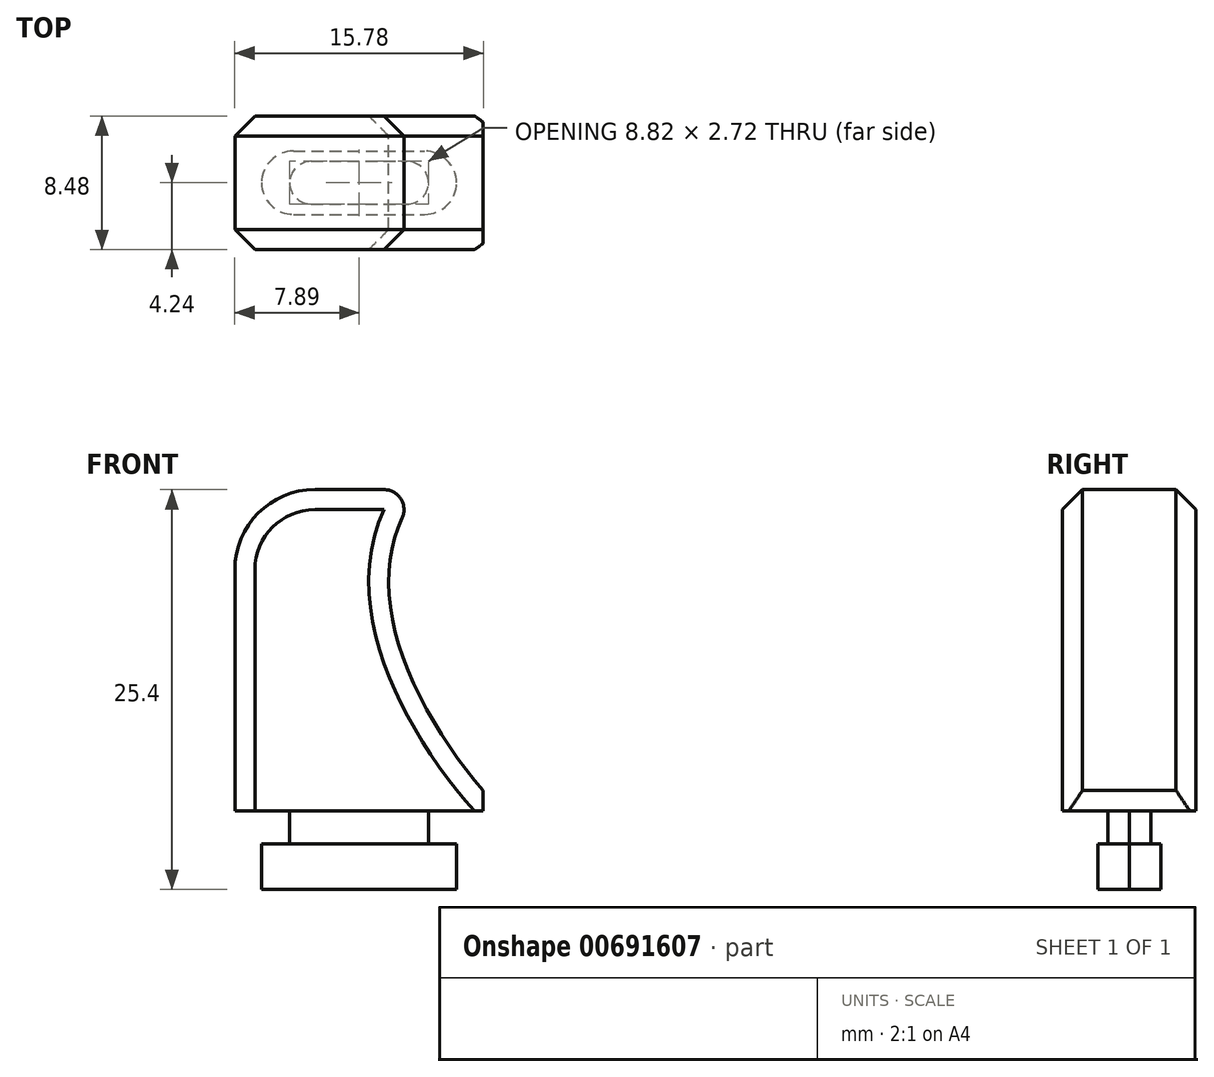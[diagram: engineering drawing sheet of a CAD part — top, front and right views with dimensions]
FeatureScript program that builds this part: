
annotation { "Feature Type Name" : "Feature", "Feature Type Description" : "" }
export const myFeature = defineFeature(function(context is Context, id is Id, definition is map)
    precondition{}
    {
        {
            var Q0;
            Q0=qCreatedBy(makeId("Top.planeOp"),FACE);
            var sketch = newSketch(context, id + "F0", { "sketchPlane" : qUnion([Q0])});
            skLineSegment(sketch, "E0.bottom", {"start": v(-6.2, -2) * mm, "end": v(6.2, -2) * mm});
            skLineSegment(sketch, "E0.top", {"start": v(-6.2, 2) * mm, "end": v(6.2, 2) * mm});
            skLineSegment(sketch, "E0.left", {"start": v(-6.2, -2) * mm, "end": v(-6.2, 2) * mm});
            skLineSegment(sketch, "E0.right", {"start": v(6.2, -2) * mm, "end": v(6.2, 2) * mm});
            skPoint(sketch, "E0.middle", {"position": v(0, 0) * mm});
            skSolve(sketch);
        }
        {
            var Q0;
            Q0=makeQuery(id+"F0.imprint","IMPRINT",FACE,{"disambiguationData":[TD([[makeQuery(id+"F0.imprint","IMPRINT",EDGE,{"derivedFrom":sQuery(id+"F0.wireOp",EDGE,"E0.bottom")}),1.0]])]});
            extrude(context, id + "F1", {"entities" : qUnion([Q0]), "depth" : 2.9 * mm, "offsetDistance" : 25.4 * mm});
        }
        {
            var Q0;
            Q0=makeQuery(id+"F1.opExtrude","SWEPT_EDGE",EDGE,{"disambiguationData":[OSD([sQuery(id+"F0.wireOp",EDGE,"E0.top"),sQuery(id+"F0.wireOp",EDGE,"E0.left")])]});
            var Q1;
            Q1=makeQuery(id+"F1.opExtrude","SWEPT_EDGE",EDGE,{"disambiguationData":[OSD([sQuery(id+"F0.wireOp",EDGE,"E0.bottom"),sQuery(id+"F0.wireOp",EDGE,"E0.left")])]});
            fillet(context, id + "F2", {"entities" : qUnion([Q0, Q1]), "radius" : 2.03 * mm, "tangentPropagation" : true, "allowEdgeOverflow" : false});
        }
        {
            var Q0;
            Q0=makeQuery(id+"F1.opExtrude","SWEPT_EDGE",EDGE,{"disambiguationData":[OSD([sQuery(id+"F0.wireOp",EDGE,"E0.top"),sQuery(id+"F0.wireOp",EDGE,"E0.right")])]});
            var Q1;
            Q1=makeQuery(id+"F1.opExtrude","SWEPT_EDGE",EDGE,{"disambiguationData":[OSD([sQuery(id+"F0.wireOp",EDGE,"E0.bottom"),sQuery(id+"F0.wireOp",EDGE,"E0.right")])]});
            fillet(context, id + "F3", {"entities" : qUnion([Q0, Q1]), "radius" : 2.03 * mm, "tangentPropagation" : true, "allowEdgeOverflow" : false});
        }
        {
            var Q0;
            Q0=makeQuery(id+"F1.opExtrude","CAP_FACE",FACE,{"disambiguationData":[OSD([sQuery(id+"F0.wireOp",EDGE,"E0.bottom"),sQuery(id+"F0.wireOp",EDGE,"E0.top"),sQuery(id+"F0.wireOp",EDGE,"E0.left"),sQuery(id+"F0.wireOp",EDGE,"E0.right")])],"isStart":false});
            var sketch = newSketch(context, id + "F4", { "sketchPlane" : qUnion([Q0])});
            skLineSegment(sketch, "E1.bottom", {"start": v(-4.4, -1.36) * mm, "end": v(4.4, -1.36) * mm});
            skLineSegment(sketch, "E1.top", {"start": v(-4.4, 1.36) * mm, "end": v(4.4, 1.36) * mm});
            skLineSegment(sketch, "E1.left", {"start": v(-4.4, -1.36) * mm, "end": v(-4.4, 1.36) * mm});
            skLineSegment(sketch, "E1.right", {"start": v(4.4, -1.36) * mm, "end": v(4.4, 1.36) * mm});
            skPoint(sketch, "E1.middle", {"position": v(0, 0) * mm});
            skSolve(sketch);
        }
        {
            var Q0;
            Q0=makeQuery(id+"F4.imprint","IMPRINT",FACE,{"disambiguationData":[TD([[makeQuery(id+"F4.imprint","IMPRINT",EDGE,{"derivedFrom":sQuery(id+"F4.wireOp",EDGE,"E1.bottom")}),1.0]])]});
            extrude(context, id + "F5", {"entities" : qUnion([Q0]), "operationType" : NewBodyOperationType.ADD, "depth" : 2.1 * mm, "offsetDistance" : 25.4 * mm});
        }
        {
            var Q0;
            Q0=makeQuery(id+"F5.opExtrude","SWEPT_EDGE",EDGE,{"disambiguationData":[OSD([sQuery(id+"F4.wireOp",EDGE,"E1.bottom"),sQuery(id+"F4.wireOp",EDGE,"E1.left")])]});
            var Q1;
            Q1=makeQuery(id+"F5.opExtrude","SWEPT_EDGE",EDGE,{"disambiguationData":[OSD([sQuery(id+"F4.wireOp",EDGE,"E1.top"),sQuery(id+"F4.wireOp",EDGE,"E1.left")])]});
            fillet(context, id + "F6", {"entities" : qUnion([Q0, Q1]), "radius" : 1.37 * mm, "tangentPropagation" : true, "allowEdgeOverflow" : false});
        }
        {
            var Q0;
            Q0=makeQuery(id+"F5.opExtrude","SWEPT_EDGE",EDGE,{"disambiguationData":[OSD([sQuery(id+"F4.wireOp",EDGE,"E1.top"),sQuery(id+"F4.wireOp",EDGE,"E1.right")])]});
            var Q1;
            Q1=makeQuery(id+"F5.opExtrude","SWEPT_EDGE",EDGE,{"disambiguationData":[OSD([sQuery(id+"F4.wireOp",EDGE,"E1.bottom"),sQuery(id+"F4.wireOp",EDGE,"E1.right")])]});
            fillet(context, id + "F7", {"entities" : qUnion([Q0, Q1]), "radius" : 1.37 * mm, "tangentPropagation" : true, "allowEdgeOverflow" : false});
        }
        {
            var Q0;
            Q0=qCreatedBy(makeId("Top.planeOp"),FACE);
            var sketch = newSketch(context, id + "F8", { "sketchPlane" : qUnion([Q0])});
            skLineSegment(sketch, "E2.bottom", {"start": v(-7.89, -4.24) * mm, "end": v(7.89, -4.24) * mm});
            skLineSegment(sketch, "E2.top", {"start": v(-7.89, 4.24) * mm, "end": v(7.89, 4.24) * mm});
            skLineSegment(sketch, "E2.left", {"start": v(-7.89, -4.24) * mm, "end": v(-7.89, 4.24) * mm});
            skLineSegment(sketch, "E2.right", {"start": v(7.89, -4.24) * mm, "end": v(7.89, 4.24) * mm});
            skPoint(sketch, "E2.middle", {"position": v(0, 0) * mm});
            skSolve(sketch);
        }
        {
            var Q0;
            Q0=makeQuery(id+"F8.imprint","IMPRINT",FACE,{"disambiguationData":[TD([[makeQuery(id+"F8.imprint","IMPRINT",EDGE,{"derivedFrom":sQuery(id+"F8.wireOp",EDGE,"E2.bottom")}),1.0]])]});
            extrude(context, id + "F9", {"entities" : qUnion([Q0]), "operationType" : NewBodyOperationType.ADD, "depth" : 25.4 * mm, "offsetDistance" : 25.4 * mm, "hasSecondDirection" : true, "secondDirectionOppositeDirection" : false, "secondDirectionDepth" : 5 * mm});
        }
        {
            var Q0;
            Q0=qCreatedBy(makeId("Front.planeOp"),FACE);
            var sketch = newSketch(context, id + "F10", { "sketchPlane" : qUnion([Q0])});
            skFitSpline(sketch, "E3", {"points": [v(4.8, 26.41) * mm, v(2.47, 15.73) * mm, v(11.26, 3.33) * mm, v(13.6, 3.08) * mm, v(13.85, 5.6) * mm, v(12.97, 27.36) * mm, v(4.8, 26.41) * mm]});
            skSolve(sketch);
        }
        {
            var Q0;
            Q0=makeQuery(id+"F10.imprint","IMPRINT",FACE,{"disambiguationData":[TD([[makeQuery(id+"F10.imprint","IMPRINT",EDGE,{"derivedFrom":sQuery(id+"F10.wireOp",EDGE,"E3")}),1.0]])]});
            extrude(context, id + "F11", {"entities" : qUnion([Q0]), "operationType" : NewBodyOperationType.REMOVE, "oppositeDirection" : true, "depth" : 25.4 * mm, "offsetDistance" : 25.4 * mm, "hasSecondDirection" : true, "secondDirectionOppositeDirection" : false, "secondDirectionDepth" : 25.4 * mm});
        }
        {
            var Q0;
            Q0=makeQuery(id+"F11.boolean.opBoolean","INTERSECT",EDGE,{"derivedFrom":[makeQuery(id+"F9.opExtrude","CAP_FACE",FACE,{"disambiguationData":[OSD([sQuery(id+"F8.wireOp",EDGE,"E2.bottom"),sQuery(id+"F8.wireOp",EDGE,"E2.top"),sQuery(id+"F8.wireOp",EDGE,"E2.left"),sQuery(id+"F8.wireOp",EDGE,"E2.right")])],"isStart":false}),makeQuery(id+"F11.opExtrude","SWEPT_FACE",FACE,{"disambiguationData":[OSD([sQuery(id+"F10.wireOp",EDGE,"E3")])]})]});
            fillet(context, id + "F12", {"entities" : qUnion([Q0]), "radius" : 1.27 * mm, "tangentPropagation" : true, "allowEdgeOverflow" : false});
        }
        {
            var Q0;
            Q0=makeQuery(id+"F9.opExtrude","CAP_EDGE",EDGE,{"disambiguationData":[OSD([sQuery(id+"F8.wireOp",EDGE,"E2.left")])],"isStart":false});
            fillet(context, id + "F13", {"entities" : qUnion([Q0]), "radius" : 5.08 * mm, "tangentPropagation" : true, "allowEdgeOverflow" : false});
        }
        {
            var Q0;
            Q0=makeQuery(id+"F11.boolean.opBoolean","INTERSECT",EDGE,{"derivedFrom":[makeQuery(id+"F9.opExtrude","SWEPT_FACE",FACE,{"disambiguationData":[OSD([sQuery(id+"F8.wireOp",EDGE,"E2.bottom")])]}),makeQuery(id+"F11.opExtrude","SWEPT_FACE",FACE,{"disambiguationData":[OSD([sQuery(id+"F10.wireOp",EDGE,"E3")])]})]});
            chamfer(context, id + "F14", {"entities" : qUnion([Q0]), "width" : 1.27 * mm, "tangentPropagation" : true});
        }
        {
            var Q0;
            Q0=makeQuery(id+"F11.boolean.opBoolean","INTERSECT",EDGE,{"derivedFrom":[makeQuery(id+"F9.opExtrude","SWEPT_FACE",FACE,{"disambiguationData":[OSD([sQuery(id+"F8.wireOp",EDGE,"E2.top")])]}),makeQuery(id+"F11.opExtrude","SWEPT_FACE",FACE,{"disambiguationData":[OSD([sQuery(id+"F10.wireOp",EDGE,"E3")])]})]});
            chamfer(context, id + "F15", {"entities" : qUnion([Q0]), "width" : 1.27 * mm, "tangentPropagation" : true});
        }
    });
